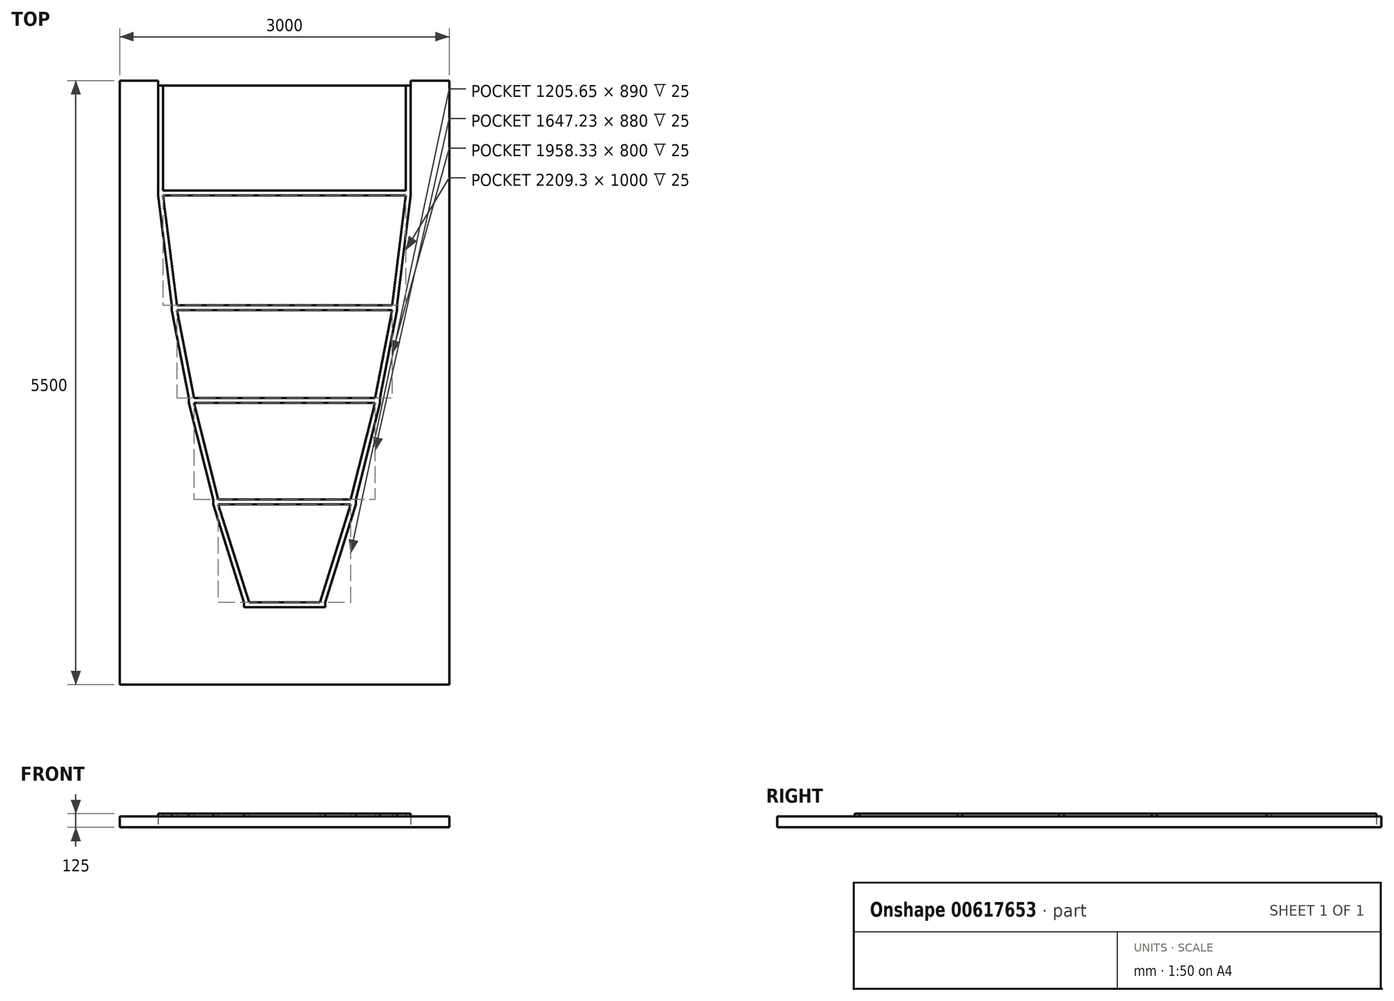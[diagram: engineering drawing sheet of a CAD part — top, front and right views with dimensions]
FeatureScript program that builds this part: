
annotation { "Feature Type Name" : "Feature", "Feature Type Description" : "" }
export const myFeature = defineFeature(function(context is Context, id is Id, definition is map)
    precondition{}
    {
        {
            var Q0;
            Q0=qCreatedBy(makeId("Top.planeOp"),FACE);
            var sketch = newSketch(context, id + "F0", { "sketchPlane" : qUnion([Q0])});
            skLineSegment(sketch, "E0.bottom", {"start": v(1500, 2912.5) * mm, "end": v(-1500, 2912.5) * mm});
            skLineSegment(sketch, "E0.top", {"start": v(1500, -2587.5) * mm, "end": v(-1500, -2587.5) * mm});
            skLineSegment(sketch, "E0.left", {"start": v(1500, 2912.5) * mm, "end": v(1500, -2587.5) * mm});
            skLineSegment(sketch, "E0.right", {"start": v(-1500, 2912.5) * mm, "end": v(-1500, -2587.5) * mm});
            skLineSegment(sketch, "E1.bottom", {"start": v(-1500, -2587.5) * mm, "end": v(1500, -2587.5) * mm});
            skLineSegment(sketch, "E1.left", {"start": v(-1500, -2587.5) * mm, "end": v(-1500, -1587.5) * mm});
            skLineSegment(sketch, "E1.right", {"start": v(1500, -2587.5) * mm, "end": v(1500, -1587.5) * mm});
            skLineSegment(sketch, "E2.bottom", {"start": v(1150, 1912.5) * mm, "end": v(-1150, 1912.5) * mm});
            skLineSegment(sketch, "E2.top", {"start": v(1150, 1867.5) * mm, "end": v(-1150, 1867.5) * mm});
            skLineSegment(sketch, "E2.left", {"start": v(1150, 1912.5) * mm, "end": v(1150, 1867.5) * mm});
            skLineSegment(sketch, "E2.right", {"start": v(-1150, 1912.5) * mm, "end": v(-1150, 1867.5) * mm});
            skPoint(sketch, "E2.middle", {"position": v(0, 1890) * mm});
            skPoint(sketch, "E3.middle", {"position": v(0, 935.36) * mm});
            skLineSegment(sketch, "E4.bottom", {"start": v(1025, 822.5) * mm, "end": v(-1025, 822.5) * mm});
            skLineSegment(sketch, "E4.top", {"start": v(1025, 867.5) * mm, "end": v(-1025, 867.5) * mm});
            skLineSegment(sketch, "E4.left", {"start": v(1025, 822.5) * mm, "end": v(1025, 867.5) * mm});
            skLineSegment(sketch, "E4.right", {"start": v(-1025, 822.5) * mm, "end": v(-1025, 867.5) * mm});
            skPoint(sketch, "E4.middle", {"position": v(0, 845) * mm});
            skLineSegment(sketch, "E5.bottom", {"start": v(870, -22.5) * mm, "end": v(-870, -22.5) * mm});
            skLineSegment(sketch, "E5.top", {"start": v(870, 22.5) * mm, "end": v(-870, 22.5) * mm});
            skLineSegment(sketch, "E5.left", {"start": v(870, -22.5) * mm, "end": v(870, 22.5) * mm});
            skLineSegment(sketch, "E5.right", {"start": v(-870, -22.5) * mm, "end": v(-870, 22.5) * mm});
            skPoint(sketch, "E5.middle", {"position": v(0, 0) * mm});
            skLineSegment(sketch, "E6.bottom", {"start": v(650, -947.5) * mm, "end": v(-650, -947.5) * mm});
            skLineSegment(sketch, "E6.top", {"start": v(650, -902.5) * mm, "end": v(-650, -902.5) * mm});
            skLineSegment(sketch, "E6.left", {"start": v(650, -947.5) * mm, "end": v(650, -902.5) * mm});
            skLineSegment(sketch, "E6.right", {"start": v(-650, -947.5) * mm, "end": v(-650, -902.5) * mm});
            skPoint(sketch, "E6.middle", {"position": v(0, -925) * mm});
            skLineSegment(sketch, "E7.bottom", {"start": v(370, -1882.5) * mm, "end": v(-370, -1882.5) * mm});
            skLineSegment(sketch, "E7.top", {"start": v(370, -1837.5) * mm, "end": v(-370, -1837.5) * mm});
            skLineSegment(sketch, "E7.left", {"start": v(370, -1882.5) * mm, "end": v(370, -1837.5) * mm});
            skLineSegment(sketch, "E7.right", {"start": v(-370, -1882.5) * mm, "end": v(-370, -1837.5) * mm});
            skPoint(sketch, "E7.middle", {"position": v(0, -1860) * mm});
            skLineSegment(sketch, "E8.bottom", {"start": v(-1150, 2912.5) * mm, "end": v(1150, 2912.5) * mm});
            skLineSegment(sketch, "E8.top", {"start": v(-1150, 2867.5) * mm, "end": v(1150, 2867.5) * mm});
            skLineSegment(sketch, "E8.left", {"start": v(-1150, 2912.5) * mm, "end": v(-1150, 2867.5) * mm});
            skLineSegment(sketch, "E8.right", {"start": v(1150, 2912.5) * mm, "end": v(1150, 2867.5) * mm});
            skPoint(sketch, "E8.middle", {"position": v(0, 2890) * mm});
            skLineSegment(sketch, "E9", {"start": v(-370, -1837.5) * mm, "end": v(-650, -947.5) * mm});
            skLineSegment(sketch, "E10", {"start": v(-602.83, -947.5) * mm, "end": v(-322.83, -1837.5) * mm});
            skLineSegment(sketch, "E11.MirrorCS", {"start": v(602.83, -947.5) * mm, "end": v(322.83, -1837.5) * mm});
            skLineSegment(sketch, "E12.MirrorCS", {"start": v(370, -1837.5) * mm, "end": v(650, -947.5) * mm});
            skLineSegment(sketch, "E13", {"start": v(-650, -902.5) * mm, "end": v(-870, -22.5) * mm});
            skLineSegment(sketch, "E14", {"start": v(-823.62, -22.5) * mm, "end": v(-603.62, -902.5) * mm});
            skLineSegment(sketch, "E15", {"start": v(-870, 22.5) * mm, "end": v(-1025, 822.5) * mm});
            skLineSegment(sketch, "E16", {"start": v(-824.16, 22.5) * mm, "end": v(-979.16, 822.5) * mm});
            skLineSegment(sketch, "E17", {"start": v(-1025, 867.5) * mm, "end": v(-1150, 1867.5) * mm});
            skLineSegment(sketch, "E18", {"start": v(-979.65, 867.5) * mm, "end": v(-1104.65, 1867.5) * mm});
            skLineSegment(sketch, "E19", {"start": v(-1150, 2867.5) * mm, "end": v(-1150, 1912.5) * mm});
            skLineSegment(sketch, "E20", {"start": v(-1105, 2867.5) * mm, "end": v(-1105, 1912.5) * mm});
            skLineSegment(sketch, "E21.MirrorCS", {"start": v(1105, 2867.5) * mm, "end": v(1105, 1912.5) * mm});
            skLineSegment(sketch, "E22.MirrorCS", {"start": v(1150, 2867.5) * mm, "end": v(1150, 1912.5) * mm});
            skLineSegment(sketch, "E23.MirrorCS", {"start": v(979.65, 867.5) * mm, "end": v(1104.65, 1867.5) * mm});
            skLineSegment(sketch, "E24.MirrorCS", {"start": v(1025, 867.5) * mm, "end": v(1150, 1867.5) * mm});
            skLineSegment(sketch, "E25.MirrorCS", {"start": v(824.16, 22.5) * mm, "end": v(979.16, 822.5) * mm});
            skLineSegment(sketch, "E26.MirrorCS", {"start": v(870, 22.5) * mm, "end": v(1025, 822.5) * mm});
            skLineSegment(sketch, "E27.MirrorCS", {"start": v(650, -902.5) * mm, "end": v(870, -22.5) * mm});
            skLineSegment(sketch, "E28.MirrorCS", {"start": v(823.62, -22.5) * mm, "end": v(603.62, -902.5) * mm});
            skSolve(sketch);
        }
        {
            var Q0;
            Q0=makeQuery(id+"F0.imprint","IMPRINT",FACE,{"disambiguationData":[TD([[makeQuery(id+"F0.imprint","IMPRINT",EDGE,{"derivedFrom":sQuery(id+"F0.wireOp",EDGE,"E0.bottom")}),1.0]])]});
            var Q1;
            {var subQ5=sQuery(id+"F0.wireOp",EDGE,"E3.top");Q1=makeQuery(id+"F0.imprint","IMPRINT",FACE,{"disambiguationData":[TD([[makeQuery(id+"F0.imprint","IMPRINT",EDGE,{"derivedFrom":subQ5}),-1.0]])]});}
            var Q2;
            Q2=makeQuery(id+"F0.imprint","IMPRINT",FACE,{"disambiguationData":[TD([[makeQuery(id+"F0.imprint","IMPRINT",EDGE,{"derivedFrom":sQuery(id+"F0.wireOp",EDGE,"YqaG7ZQv-Sa8W-aPUu-p3km-sfK5Fq0OgX0M.bottom")}),1.0]])]});
            var Q3;
            Q3=makeQuery(id+"F0.imprint","IMPRINT",FACE,{"disambiguationData":[TD([[makeQuery(id+"F0.imprint","IMPRINT",EDGE,{"derivedFrom":sQuery(id+"F0.wireOp",EDGE,"iPejV9fT-LI6E-AjAW-6P53-3hMjtixCcsEi.bottom")}),1.0]])]});
            var Q4;
            Q4=makeQuery(id+"F0.imprint","IMPRINT",FACE,{"disambiguationData":[TD([[makeQuery(id+"F0.imprint","IMPRINT",EDGE,{"derivedFrom":sQuery(id+"F0.wireOp",EDGE,"i1mdIKdA-ZCbR-lqWo-f0Yo-Ub5HT9tBqHFv.bottom")}),1.0]])]});
            var Q5;
            Q5=makeQuery(id+"F0.imprint","IMPRINT",FACE,{"disambiguationData":[TD([[makeQuery(id+"F0.imprint","IMPRINT",EDGE,{"derivedFrom":sQuery(id+"F0.wireOp",EDGE,"3BLmCjpf-GRli-MI8m-OWfn-ilBZLSlzRN9N.bottom")}),1.0]])]});
            var Q6;
            Q6=makeQuery(id+"F0.imprint","IMPRINT",FACE,{"disambiguationData":[TD([[makeQuery(id+"F0.imprint","IMPRINT",EDGE,{"derivedFrom":sQuery(id+"F0.wireOp",EDGE,"E1.bottom")}),1.0]])]});
            var Q7;
            {var subQ0=sQuery(id+"F0.wireOp",EDGE,"E10");Q7=makeQuery(id+"F0.imprint","IMPRINT",FACE,{"disambiguationData":[TD([[makeQuery(id+"F0.imprint","IMPRINT",EDGE,{"derivedFrom":subQ0}),1.0]])]});}
            var Q8;
            {var subQ0=sQuery(id+"F0.wireOp",EDGE,"E9");Q8=makeQuery(id+"F0.imprint","IMPRINT",FACE,{"disambiguationData":[TD([[makeQuery(id+"F0.imprint","IMPRINT",EDGE,{"derivedFrom":subQ0}),-1.0]])]});}
            var Q9;
            {var subQ2=sQuery(id+"F0.wireOp",EDGE,"E11.MirrorCS");Q9=makeQuery(id+"F0.imprint","IMPRINT",FACE,{"disambiguationData":[TD([[makeQuery(id+"F0.imprint","IMPRINT",EDGE,{"derivedFrom":subQ2}),1.0]])]});}
            var Q10;
            {var subQ0=sQuery(id+"F0.wireOp",EDGE,"E14");Q10=makeQuery(id+"F0.imprint","IMPRINT",FACE,{"disambiguationData":[TD([[makeQuery(id+"F0.imprint","IMPRINT",EDGE,{"derivedFrom":subQ0}),1.0]])]});}
            var Q11;
            {var subQ0=sQuery(id+"F0.wireOp",EDGE,"E13");Q11=makeQuery(id+"F0.imprint","IMPRINT",FACE,{"disambiguationData":[TD([[makeQuery(id+"F0.imprint","IMPRINT",EDGE,{"derivedFrom":subQ0}),-1.0]])]});}
            var Q12;
            {var subQ0=sQuery(id+"F0.wireOp",EDGE,"E5.left");Q12=makeQuery(id+"F0.imprint","IMPRINT",FACE,{"disambiguationData":[TD([[makeQuery(id+"F0.imprint","IMPRINT",EDGE,{"derivedFrom":subQ0}),1.0]])]});}
            var Q13;
            {var subQ0=sQuery(id+"F0.wireOp",EDGE,"E27.MirrorCS");Q13=makeQuery(id+"F0.imprint","IMPRINT",FACE,{"disambiguationData":[TD([[makeQuery(id+"F0.imprint","IMPRINT",EDGE,{"derivedFrom":subQ0}),1.0]])]});}
            var Q14;
            {var subQ2=sQuery(id+"F0.wireOp",EDGE,"E25.MirrorCS");Q14=makeQuery(id+"F0.imprint","IMPRINT",FACE,{"disambiguationData":[TD([[makeQuery(id+"F0.imprint","IMPRINT",EDGE,{"derivedFrom":subQ2}),-1.0]])]});}
            var Q15;
            {var subQ0=sQuery(id+"F0.wireOp",EDGE,"E16");Q15=makeQuery(id+"F0.imprint","IMPRINT",FACE,{"disambiguationData":[TD([[makeQuery(id+"F0.imprint","IMPRINT",EDGE,{"derivedFrom":subQ0}),-1.0]])]});}
            var Q16;
            {var subQ0=sQuery(id+"F0.wireOp",EDGE,"E15");Q16=makeQuery(id+"F0.imprint","IMPRINT",FACE,{"disambiguationData":[TD([[makeQuery(id+"F0.imprint","IMPRINT",EDGE,{"derivedFrom":subQ0}),-1.0]])]});}
            var Q17;
            {var subQ0=sQuery(id+"F0.wireOp",EDGE,"E4.left");Q17=makeQuery(id+"F0.imprint","IMPRINT",FACE,{"disambiguationData":[TD([[makeQuery(id+"F0.imprint","IMPRINT",EDGE,{"derivedFrom":subQ0}),1.0]])]});}
            var Q18;
            {var subQ0=sQuery(id+"F0.wireOp",EDGE,"E18");Q18=makeQuery(id+"F0.imprint","IMPRINT",FACE,{"disambiguationData":[TD([[makeQuery(id+"F0.imprint","IMPRINT",EDGE,{"derivedFrom":subQ0}),-1.0]])]});}
            var Q19;
            {var subQ2=sQuery(id+"F0.wireOp",EDGE,"E23.MirrorCS");Q19=makeQuery(id+"F0.imprint","IMPRINT",FACE,{"disambiguationData":[TD([[makeQuery(id+"F0.imprint","IMPRINT",EDGE,{"derivedFrom":subQ2}),-1.0]])]});}
            var Q20;
            {var subQ0=sQuery(id+"F0.wireOp",EDGE,"E2.left");Q20=makeQuery(id+"F0.imprint","IMPRINT",FACE,{"disambiguationData":[TD([[makeQuery(id+"F0.imprint","IMPRINT",EDGE,{"derivedFrom":subQ0}),-1.0]])]});}
            var Q21;
            {var subQ0=sQuery(id+"F0.wireOp",EDGE,"E17");Q21=makeQuery(id+"F0.imprint","IMPRINT",FACE,{"disambiguationData":[TD([[makeQuery(id+"F0.imprint","IMPRINT",EDGE,{"derivedFrom":subQ0}),-1.0]])]});}
            var Q22;
            {var subQ0=sQuery(id+"F0.wireOp",EDGE,"E20");Q22=makeQuery(id+"F0.imprint","IMPRINT",FACE,{"disambiguationData":[TD([[makeQuery(id+"F0.imprint","IMPRINT",EDGE,{"derivedFrom":subQ0}),1.0]])]});}
            var Q23;
            {var subQ2=sQuery(id+"F0.wireOp",EDGE,"E21.MirrorCS");Q23=makeQuery(id+"F0.imprint","IMPRINT",FACE,{"disambiguationData":[TD([[makeQuery(id+"F0.imprint","IMPRINT",EDGE,{"derivedFrom":subQ2}),1.0]])]});}
            var Q24;
            Q24=makeQuery(id+"F0.imprint","IMPRINT",FACE,{"disambiguationData":[TD([[makeQuery(id+"F0.imprint","IMPRINT",EDGE,{"derivedFrom":sQuery(id+"F0.wireOp",EDGE,"E8.bottom")}),-1.0]])]});
            var Q25;
            {var subQ0=sQuery(id+"F0.wireOp",EDGE,"E19");Q25=makeQuery(id+"F0.imprint","IMPRINT",FACE,{"disambiguationData":[TD([[makeQuery(id+"F0.imprint","IMPRINT",EDGE,{"derivedFrom":subQ0}),1.0]])]});}
            var Q26;
            {var subQ0=sQuery(id+"F0.wireOp",EDGE,"E6.left");Q26=makeQuery(id+"F0.imprint","IMPRINT",FACE,{"disambiguationData":[TD([[makeQuery(id+"F0.imprint","IMPRINT",EDGE,{"derivedFrom":subQ0}),1.0]])]});}
            var Q27;
            Q27=makeQuery(id+"F0.imprint","IMPRINT",FACE,{"disambiguationData":[TD([[makeQuery(id+"F0.imprint","IMPRINT",EDGE,{"derivedFrom":sQuery(id+"F0.wireOp",EDGE,"E7.bottom")}),-1.0]])]});
            extrude(context, id + "F1", {"entities" : qUnion([Q0, Q1, Q2, Q3, Q4, Q5, Q6, Q7, Q8, Q9, Q10, Q11, Q12, Q13, Q14, Q15, Q16, Q17, Q18, Q19, Q20, Q21, Q22, Q23, Q24, Q25, Q26, Q27]), "depth" : 100 * mm, "offsetDistance" : 25 * mm});
        }
        {
            var Q0;
            Q0=makeQuery(id+"F0.imprint","IMPRINT",FACE,{"disambiguationData":[TD([[makeQuery(id+"F0.imprint","IMPRINT",EDGE,{"derivedFrom":sQuery(id+"F0.wireOp",EDGE,"E2.bottom")}),1.0]])]});
            var Q1;
            Q1=makeQuery(id+"F0.imprint","IMPRINT",FACE,{"disambiguationData":[TD([[makeQuery(id+"F0.imprint","IMPRINT",EDGE,{"derivedFrom":sQuery(id+"F0.wireOp",EDGE,"E4.bottom")}),-1.0]])]});
            var Q2;
            Q2=makeQuery(id+"F0.imprint","IMPRINT",FACE,{"disambiguationData":[TD([[makeQuery(id+"F0.imprint","IMPRINT",EDGE,{"derivedFrom":sQuery(id+"F0.wireOp",EDGE,"E5.bottom")}),-1.0]])]});
            var Q3;
            Q3=makeQuery(id+"F0.imprint","IMPRINT",FACE,{"disambiguationData":[TD([[makeQuery(id+"F0.imprint","IMPRINT",EDGE,{"derivedFrom":sQuery(id+"F0.wireOp",EDGE,"E6.bottom")}),-1.0]])]});
            var Q4;
            Q4=makeQuery(id+"F0.imprint","IMPRINT",FACE,{"disambiguationData":[TD([[makeQuery(id+"F0.imprint","IMPRINT",EDGE,{"derivedFrom":sQuery(id+"F0.wireOp",EDGE,"E7.bottom")}),-1.0]])]});
            var Q5;
            Q5=makeQuery(id+"F0.imprint","IMPRINT",FACE,{"disambiguationData":[TD([[makeQuery(id+"F0.imprint","IMPRINT",EDGE,{"derivedFrom":sQuery(id+"F0.wireOp",EDGE,"E8.bottom")}),-1.0]])]});
            extrude(context, id + "F2", {"entities" : qUnion([Q0, Q1, Q2, Q3, Q4, Q5]), "operationType" : NewBodyOperationType.ADD, "depth" : 125 * mm, "offsetDistance" : 25 * mm});
        }
        {
            var Q0;
            {var subQ0=sQuery(id+"F0.wireOp",EDGE,"E9");Q0=makeQuery(id+"F0.imprint","IMPRINT",FACE,{"disambiguationData":[TD([[makeQuery(id+"F0.imprint","IMPRINT",EDGE,{"derivedFrom":subQ0}),-1.0]])]});}
            var Q1;
            {var subQ2=sQuery(id+"F0.wireOp",EDGE,"E11.MirrorCS");Q1=makeQuery(id+"F0.imprint","IMPRINT",FACE,{"disambiguationData":[TD([[makeQuery(id+"F0.imprint","IMPRINT",EDGE,{"derivedFrom":subQ2}),1.0]])]});}
            var Q2;
            {var subQ0=sQuery(id+"F0.wireOp",EDGE,"E13");Q2=makeQuery(id+"F0.imprint","IMPRINT",FACE,{"disambiguationData":[TD([[makeQuery(id+"F0.imprint","IMPRINT",EDGE,{"derivedFrom":subQ0}),-1.0]])]});}
            var Q3;
            {var subQ0=sQuery(id+"F0.wireOp",EDGE,"E27.MirrorCS");Q3=makeQuery(id+"F0.imprint","IMPRINT",FACE,{"disambiguationData":[TD([[makeQuery(id+"F0.imprint","IMPRINT",EDGE,{"derivedFrom":subQ0}),1.0]])]});}
            var Q4;
            {var subQ2=sQuery(id+"F0.wireOp",EDGE,"E25.MirrorCS");Q4=makeQuery(id+"F0.imprint","IMPRINT",FACE,{"disambiguationData":[TD([[makeQuery(id+"F0.imprint","IMPRINT",EDGE,{"derivedFrom":subQ2}),-1.0]])]});}
            var Q5;
            {var subQ0=sQuery(id+"F0.wireOp",EDGE,"E15");Q5=makeQuery(id+"F0.imprint","IMPRINT",FACE,{"disambiguationData":[TD([[makeQuery(id+"F0.imprint","IMPRINT",EDGE,{"derivedFrom":subQ0}),-1.0]])]});}
            var Q6;
            {var subQ2=sQuery(id+"F0.wireOp",EDGE,"E23.MirrorCS");Q6=makeQuery(id+"F0.imprint","IMPRINT",FACE,{"disambiguationData":[TD([[makeQuery(id+"F0.imprint","IMPRINT",EDGE,{"derivedFrom":subQ2}),-1.0]])]});}
            var Q7;
            {var subQ2=sQuery(id+"F0.wireOp",EDGE,"E21.MirrorCS");Q7=makeQuery(id+"F0.imprint","IMPRINT",FACE,{"disambiguationData":[TD([[makeQuery(id+"F0.imprint","IMPRINT",EDGE,{"derivedFrom":subQ2}),1.0]])]});}
            var Q8;
            {var subQ0=sQuery(id+"F0.wireOp",EDGE,"E19");Q8=makeQuery(id+"F0.imprint","IMPRINT",FACE,{"disambiguationData":[TD([[makeQuery(id+"F0.imprint","IMPRINT",EDGE,{"derivedFrom":subQ0}),1.0]])]});}
            var Q9;
            {var subQ0=sQuery(id+"F0.wireOp",EDGE,"E17");Q9=makeQuery(id+"F0.imprint","IMPRINT",FACE,{"disambiguationData":[TD([[makeQuery(id+"F0.imprint","IMPRINT",EDGE,{"derivedFrom":subQ0}),-1.0]])]});}
            extrude(context, id + "F3", {"entities" : qUnion([Q0, Q1, Q2, Q3, Q4, Q5, Q6, Q7, Q8, Q9]), "operationType" : NewBodyOperationType.ADD, "depth" : 125 * mm, "offsetDistance" : 25 * mm});
        }
    });
